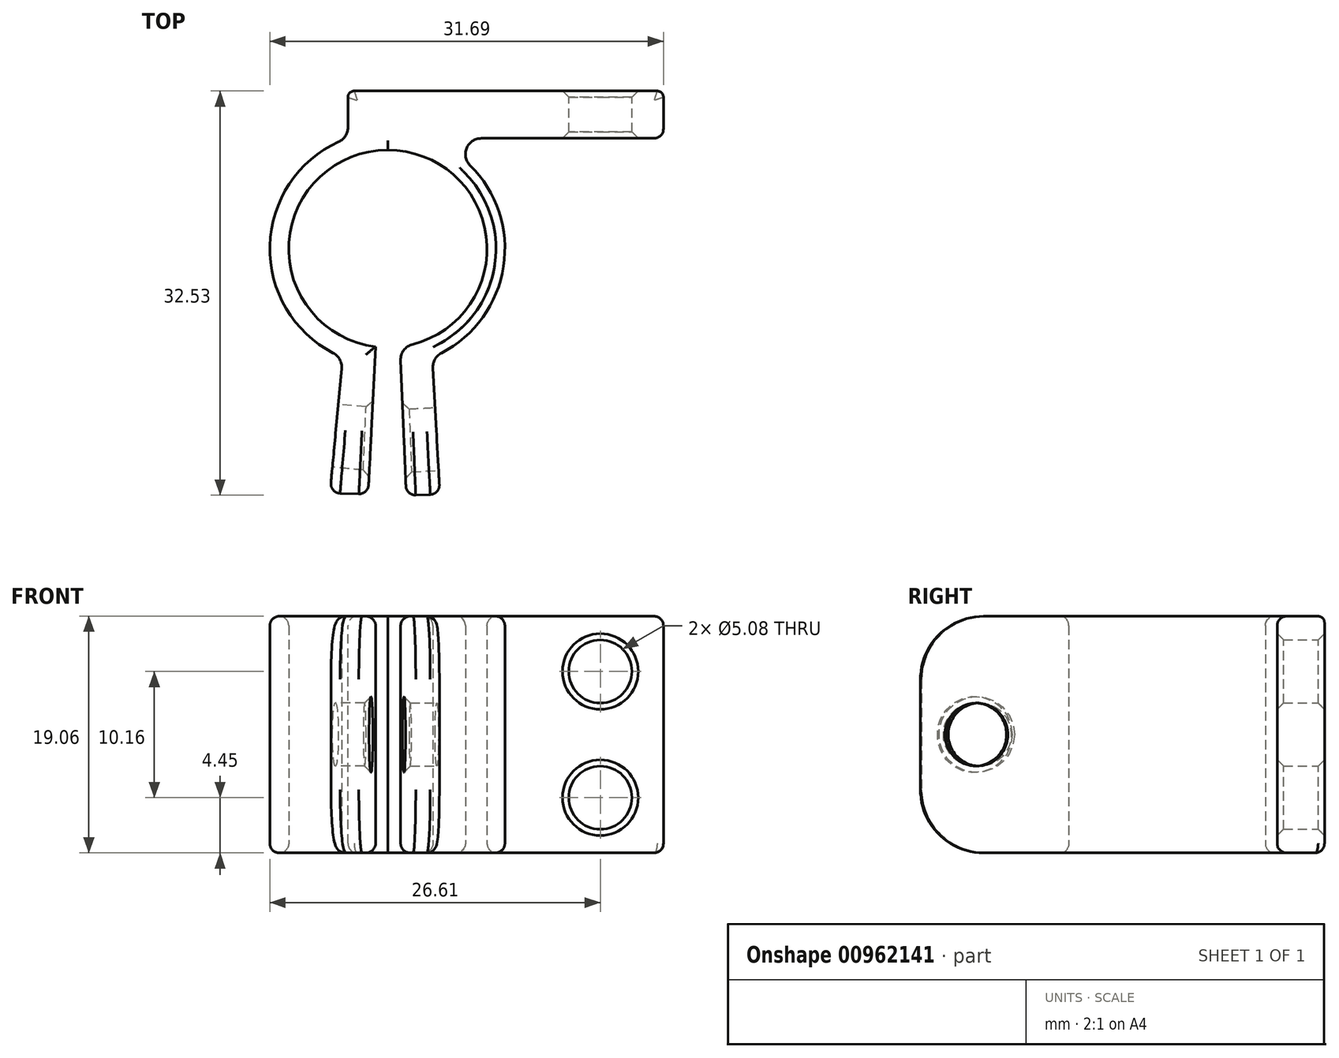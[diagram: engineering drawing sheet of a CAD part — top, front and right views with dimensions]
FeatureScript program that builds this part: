
annotation { "Feature Type Name" : "Feature", "Feature Type Description" : "" }
export const myFeature = defineFeature(function(context is Context, id is Id, definition is map)
    precondition{}
    {
        {
            var Q0;
            Q0=qCreatedBy(makeId("Front.planeOp"),FACE);
            var sketch = newSketch(context, id + "F0", { "sketchPlane" : qUnion([Q0])});
            skLineSegment(sketch, "E0.bottom", {"start": v(12.7, -9.52) * mm, "end": v(-12.7, -9.53) * mm});
            skLineSegment(sketch, "E0.top", {"start": v(12.7, 9.53) * mm, "end": v(-12.7, 9.52) * mm});
            skLineSegment(sketch, "E0.left", {"start": v(12.7, -9.52) * mm, "end": v(12.7, 9.52) * mm});
            skLineSegment(sketch, "E0.right", {"start": v(-12.7, -9.53) * mm, "end": v(-12.7, 9.53) * mm});
            skPoint(sketch, "E0.middle", {"position": v(0, 0) * mm});
            skCircle(sketch, "E1", {"center": v(7.62, 5.08) * mm, "radius": 2.54 * mm});
            skCircle(sketch, "E2.MirrorC", {"center": v(7.62, -5.08) * mm, "radius": 2.54 * mm});
            skSolve(sketch);
        }
        {
            var Q0;
            Q0 = qSketchRegion(id + "F0", true);
            extrude(context, id + "F1", {"entities" : qUnion([Q0]), "depth" : 3.8 * mm, "offsetDistance" : 25.4 * mm});
        }
        {
            var Q0;
            Q0=makeQuery(id+"F1.opExtrude","SWEPT_FACE",FACE,{"disambiguationData":[OSD([sQuery(id+"F0.wireOp",EDGE,"E0.bottom")])]});
            var sketch = newSketch(context, id + "F2", { "sketchPlane" : qUnion([Q0])});
            skLineSegment(sketch, "E3", {"start": v(-8, 32.56) * mm, "end": v(-5.3, 32.45) * mm});
            skLineSegment(sketch, "E4.trimOffspring", {"start": v(-8.5, 20.57) * mm, "end": v(-8, 32.56) * mm});
            skLineSegment(sketch, "E5.trimOffspring", {"start": v(-6, 19.81) * mm, "end": v(-6, 19.85) * mm});
            skLineSegment(sketch, "E6.MirrorCS", {"start": v(-10.47, 20.57) * mm, "end": v(-11.07, 32.46) * mm});
            skLineSegment(sketch, "E7.MirrorCS", {"start": v(-11.07, 32.46) * mm, "end": v(-14.14, 32.36) * mm});
            skLineSegment(sketch, "E8.MirrorCS", {"start": v(-12.96, 19.81) * mm, "end": v(-12.97, 19.85) * mm});
            skArc(sketch, "E9.MirrorCS", {"start": v(-8.5, 20.58) * mm, "mid": v(-1.51, 12.2) * mm, "end": v(-9.48, 4.76) * mm});
            skArc(sketch, "E10.trimOffspring", {"start": v(-13.12, 21.45) * mm, "mid": v(-9.54, 3.24) * mm, "end": v(-5.9, 21.44) * mm});
            skArc(sketch, "E11.trimOffspring", {"start": v(-10.47, 20.58) * mm, "mid": v(-17.45, 12.2) * mm, "end": v(-9.48, 4.76) * mm});
            skLineSegment(sketch, "E12.trimOffspring", {"start": v(-5.9, 21.44) * mm, "end": v(-5.3, 32.45) * mm});
            skLineSegment(sketch, "E13.trimOffspring", {"start": v(-13.12, 21.45) * mm, "end": v(-14.14, 32.36) * mm});
            skSolve(sketch);
        }
        {
            var Q0;
            Q0 = qSketchRegion(id + "F2", true);
            extrude(context, id + "F3", {"entities" : qUnion([Q0]), "operationType" : NewBodyOperationType.ADD, "oppositeDirection" : true, "depth" : 19.05 * mm, "offsetDistance" : 25.4 * mm});
        }
        {
            var Q0;
            Q0=makeQuery(id+"F3.opExtrude","SWEPT_FACE",FACE,{"disambiguationData":[OSD([sQuery(id+"F2.wireOp",EDGE,"E12.trimOffspring")])]});
            var sketch = newSketch(context, id + "F4", { "sketchPlane" : qUnion([Q0])});
            skCircle(sketch, "E14", {"center": v(-27.67, 0) * mm, "radius": 2.54 * mm});
            skPoint(sketch, "E14.centerSnap0", {"position": v(-32.11, 0) * mm});
            skSolve(sketch);
        }
        {
            var Q0;
            Q0 = qSketchRegion(id + "F4", true);
            extrude(context, id + "F5", {"entities" : qUnion([Q0]), "operationType" : NewBodyOperationType.REMOVE, "oppositeDirection" : true, "depth" : 3.17 * mm, "offsetDistance" : 25.4 * mm});
        }
        {
            var Q0;
            Q0=makeQuery(id+"F3.opExtrude","SWEPT_FACE",FACE,{"disambiguationData":[OSD([sQuery(id+"F2.wireOp",EDGE,"E13.trimOffspring")])]});
            var sketch = newSketch(context, id + "F6", { "sketchPlane" : qUnion([Q0])});
            skCircle(sketch, "E15", {"center": v(28.9, 0) * mm, "radius": 2.54 * mm});
            skSolve(sketch);
        }
        {
            var Q0;
            Q0 = qSketchRegion(id + "F6", true);
            extrude(context, id + "F7", {"entities" : qUnion([Q0]), "operationType" : NewBodyOperationType.REMOVE, "oppositeDirection" : true, "depth" : 3.17 * mm, "offsetDistance" : 25.4 * mm});
        }
        {
            var Q0;
            Q0=makeQuery(id+"F3.boolean.opBoolean","INTERSECT",EDGE,{"derivedFrom":[makeQuery(id+"F1.opExtrude","SWEPT_FACE",FACE,{"disambiguationData":[OSD([sQuery(id+"F0.wireOp",EDGE,"E0.right")])]}),makeQuery(id+"F3.opExtrude","SWEPT_FACE",FACE,{"disambiguationData":[OSD([sQuery(id+"F2.wireOp",EDGE,"E10.trimOffspring")])]})]});
            var Q1;
            Q1=makeQuery(id+"F3.opExtrude","SWEPT_EDGE",EDGE,{"disambiguationData":[OSD([sQuery(id+"F2.wireOp",EDGE,"E10.trimOffspring"),sQuery(id+"F2.wireOp",EDGE,"E13.trimOffspring")])]});
            var Q2;
            Q2=makeQuery(id+"F3.opExtrude","SWEPT_EDGE",EDGE,{"disambiguationData":[OSD([sQuery(id+"F2.wireOp",EDGE,"E4.trimOffspring"),sQuery(id+"F2.wireOp",EDGE,"E9.MirrorCS")])]});
            var Q3;
            Q3=makeQuery(id+"F3.boolean.opBoolean","INTERSECT",EDGE,{"derivedFrom":[makeQuery(id+"F1.opExtrude","CAP_FACE",FACE,{"disambiguationData":[OSD([sQuery(id+"F0.wireOp",EDGE,"E0.bottom"),sQuery(id+"F0.wireOp",EDGE,"E0.top"),sQuery(id+"F0.wireOp",EDGE,"E0.left"),sQuery(id+"F0.wireOp",EDGE,"E0.right"),sQuery(id+"F0.wireOp",EDGE,"E1"),sQuery(id+"F0.wireOp",EDGE,"E2.MirrorC")])],"isStart":false}),makeQuery(id+"F3.opExtrude","SWEPT_FACE",FACE,{"disambiguationData":[OSD([sQuery(id+"F2.wireOp",EDGE,"E10.trimOffspring")])]})]});
            var Q4;
            Q4=makeQuery(id+"F3.opExtrude","SWEPT_EDGE",EDGE,{"disambiguationData":[OSD([sQuery(id+"F2.wireOp",EDGE,"E10.trimOffspring"),sQuery(id+"F2.wireOp",EDGE,"E12.trimOffspring")])]});
            fillet(context, id + "F8", {"entities" : qUnion([Q0, Q1, Q2, Q3, Q4]), "radius" : 1.27 * mm, "tangentPropagation" : true, "allowEdgeOverflow" : false});
        }
        {
            var Q0;
            Q0=makeQuery(id+"F1.opExtrude","CAP_EDGE",EDGE,{"disambiguationData":[OSD([sQuery(id+"F0.wireOp",EDGE,"E1")])],"isStart":false});
            var Q1;
            Q1=makeQuery(id+"F1.opExtrude","CAP_EDGE",EDGE,{"disambiguationData":[OSD([sQuery(id+"F0.wireOp",EDGE,"E2.MirrorC")])],"isStart":false});
            var Q2;
            Q2=makeQuery(id+"F1.opExtrude","CAP_EDGE",EDGE,{"disambiguationData":[OSD([sQuery(id+"F0.wireOp",EDGE,"E2.MirrorC")])],"isStart":true});
            var Q3;
            Q3=makeQuery(id+"F1.opExtrude","CAP_EDGE",EDGE,{"disambiguationData":[OSD([sQuery(id+"F0.wireOp",EDGE,"E1")])],"isStart":true});
            chamfer(context, id + "F9", {"entities" : qUnion([Q0, Q1, Q2, Q3]), "width" : 0.5 * mm, "tangentPropagation" : true});
        }
        {
            var Q0;
            {var subQ0=sQuery(id+"F0.wireOp",EDGE,"E0.left");var subQ1=sQuery(id+"F0.wireOp",EDGE,"E0.bottom");Q0=makeQuery(id+"F0UlShQL8zqIgEm_1.opFillet","BLEND_EDGE",EDGE,{"blendedFrom":[makeQuery(id+"F1.opExtrude","SWEPT_EDGE",EDGE,{"disambiguationData":[OSD([subQ1,subQ0])]}),makeQuery(id+"F1.opExtrude","CAP_FACE",FACE,{"disambiguationData":[OSD([subQ1,sQuery(id+"F0.wireOp",EDGE,"E0.top"),subQ0,sQuery(id+"F0.wireOp",EDGE,"E0.right"),sQuery(id+"F0.wireOp",EDGE,"E1"),sQuery(id+"F0.wireOp",EDGE,"E2.MirrorC")])],"isStart":true})],"blendedInto":[makeQuery(id+"F1.opExtrude","CAP_FACE",FACE,{"disambiguationData":[OSD([subQ1,sQuery(id+"F0.wireOp",EDGE,"E0.top"),subQ0,sQuery(id+"F0.wireOp",EDGE,"E0.right"),sQuery(id+"F0.wireOp",EDGE,"E1"),sQuery(id+"F0.wireOp",EDGE,"E2.MirrorC")])],"isStart":true})]});}
            var Q1;
            Q1=makeQuery(id+"F1.opExtrude","CAP_EDGE",EDGE,{"disambiguationData":[OSD([sQuery(id+"F0.wireOp",EDGE,"E0.left")])],"isStart":true});
            var Q2;
            Q2=makeQuery(id+"F1.opExtrude","CAP_EDGE",EDGE,{"disambiguationData":[OSD([sQuery(id+"F0.wireOp",EDGE,"E0.top")])],"isStart":true});
            var Q3;
            Q3=makeQuery(id+"F1.opExtrude","CAP_EDGE",EDGE,{"disambiguationData":[OSD([sQuery(id+"F0.wireOp",EDGE,"E0.right")])],"isStart":true});
            var Q4;
            {var subQ0=sQuery(id+"F0.wireOp",EDGE,"E0.right");var subQ1=sQuery(id+"F0.wireOp",EDGE,"E0.bottom");Q4=makeQuery(id+"F0UlShQL8zqIgEm_1.opFillet","BLEND_EDGE",EDGE,{"blendedFrom":[makeQuery(id+"F1.opExtrude","SWEPT_EDGE",EDGE,{"disambiguationData":[OSD([subQ1,subQ0])]}),makeQuery(id+"F1.opExtrude","CAP_FACE",FACE,{"disambiguationData":[OSD([subQ1,sQuery(id+"F0.wireOp",EDGE,"E0.top"),sQuery(id+"F0.wireOp",EDGE,"E0.left"),subQ0,sQuery(id+"F0.wireOp",EDGE,"E1"),sQuery(id+"F0.wireOp",EDGE,"E2.MirrorC")])],"isStart":true})],"blendedInto":[makeQuery(id+"F1.opExtrude","CAP_FACE",FACE,{"disambiguationData":[OSD([subQ1,sQuery(id+"F0.wireOp",EDGE,"E0.top"),sQuery(id+"F0.wireOp",EDGE,"E0.left"),subQ0,sQuery(id+"F0.wireOp",EDGE,"E1"),sQuery(id+"F0.wireOp",EDGE,"E2.MirrorC")])],"isStart":true})]});}
            var Q5;
            {var subQ0=sQuery(id+"F0.wireOp",EDGE,"E0.right");var subQ1=sQuery(id+"F0.wireOp",EDGE,"E0.top");Q5=makeQuery(id+"F0UlShQL8zqIgEm_1.opFillet","BLEND_EDGE",EDGE,{"blendedFrom":[makeQuery(id+"F1.opExtrude","SWEPT_EDGE",EDGE,{"disambiguationData":[OSD([subQ1,subQ0])]}),makeQuery(id+"F1.opExtrude","CAP_FACE",FACE,{"disambiguationData":[OSD([sQuery(id+"F0.wireOp",EDGE,"E0.bottom"),subQ1,sQuery(id+"F0.wireOp",EDGE,"E0.left"),subQ0,sQuery(id+"F0.wireOp",EDGE,"E1"),sQuery(id+"F0.wireOp",EDGE,"E2.MirrorC")])],"isStart":true})],"blendedInto":[makeQuery(id+"F1.opExtrude","CAP_FACE",FACE,{"disambiguationData":[OSD([sQuery(id+"F0.wireOp",EDGE,"E0.bottom"),subQ1,sQuery(id+"F0.wireOp",EDGE,"E0.left"),subQ0,sQuery(id+"F0.wireOp",EDGE,"E1"),sQuery(id+"F0.wireOp",EDGE,"E2.MirrorC")])],"isStart":true})]});}
            fillet(context, id + "F10", {"entities" : qUnion([Q0, Q1, Q2, Q3, Q4, Q5]), "radius" : 0.5 * mm, "tangentPropagation" : true, "allowEdgeOverflow" : false});
        }
        {
            var Q0;
            Q0=makeQuery(id+"F7.boolean.opBoolean","INTERSECT",EDGE,{"derivedFrom":[makeQuery(id+"F3.opExtrude","SWEPT_FACE",FACE,{"disambiguationData":[OSD([sQuery(id+"F2.wireOp",EDGE,"E6.MirrorCS")])]}),makeQuery(id+"F7.opExtrude","SWEPT_FACE",FACE,{"disambiguationData":[OSD([sQuery(id+"F6.wireOp",EDGE,"E15")])]})]});
            var Q1;
            Q1=makeQuery(id+"F5.boolean.opBoolean","COPY",EDGE,{"derivedFrom":makeQuery(id+"F5.opExtrude","CAP_EDGE",EDGE,{"disambiguationData":[OSD([sQuery(id+"F4.wireOp",EDGE,"E14")])],"isStart":true})});
            var Q2;
            Q2=makeQuery(id+"F7.boolean.opBoolean","COPY",EDGE,{"derivedFrom":makeQuery(id+"F7.opExtrude","CAP_EDGE",EDGE,{"disambiguationData":[OSD([sQuery(id+"F6.wireOp",EDGE,"E15")])],"isStart":true})});
            var Q3;
            Q3=makeQuery(id+"F5.boolean.opBoolean","INTERSECT",EDGE,{"derivedFrom":[makeQuery(id+"F3.opExtrude","SWEPT_FACE",FACE,{"disambiguationData":[OSD([sQuery(id+"F2.wireOp",EDGE,"E4.trimOffspring")])]}),makeQuery(id+"F5.opExtrude","SWEPT_FACE",FACE,{"disambiguationData":[OSD([sQuery(id+"F4.wireOp",EDGE,"E14")])]})]});
            chamfer(context, id + "F11", {"entities" : qUnion([Q0, Q1, Q2, Q3]), "width" : 0.5 * mm, "tangentPropagation" : true});
        }
        {
            var Q0;
            Q0=makeQuery(id+"F3.opExtrude","CAP_EDGE",EDGE,{"disambiguationData":[OSD([sQuery(id+"F2.wireOp",EDGE,"E7.MirrorCS")])],"isStart":true});
            var Q1;
            Q1=makeQuery(id+"F3.opExtrude","CAP_EDGE",EDGE,{"disambiguationData":[OSD([sQuery(id+"F2.wireOp",EDGE,"E3")])],"isStart":true});
            var Q2;
            Q2=makeQuery(id+"F3.opExtrude","CAP_EDGE",EDGE,{"disambiguationData":[OSD([sQuery(id+"F2.wireOp",EDGE,"E7.MirrorCS")])],"isStart":false});
            var Q3;
            Q3=makeQuery(id+"F3.opExtrude","CAP_EDGE",EDGE,{"disambiguationData":[OSD([sQuery(id+"F2.wireOp",EDGE,"E3")])],"isStart":false});
            fillet(context, id + "F12", {"entities" : qUnion([Q0, Q1, Q2, Q3]), "radius" : 5.08 * mm, "tangentPropagation" : true, "allowEdgeOverflow" : false});
        }
        {
            var Q0;
            Q0=makeQuery(id+"F3.boolean.opBoolean","MERGE",FACE,{"derivedFrom":[makeQuery(id+"F1.opExtrude","SWEPT_FACE",FACE,{"disambiguationData":[OSD([sQuery(id+"F0.wireOp",EDGE,"E0.top")])]}),makeQuery(id+"F3.opExtrude","CAP_FACE",FACE,{"disambiguationData":[OSD([sQuery(id+"F2.wireOp",EDGE,"E3"),sQuery(id+"F2.wireOp",EDGE,"E4.trimOffspring"),sQuery(id+"F2.wireOp",EDGE,"E6.MirrorCS"),sQuery(id+"F2.wireOp",EDGE,"E7.MirrorCS"),sQuery(id+"F2.wireOp",EDGE,"E9.MirrorCS"),sQuery(id+"F2.wireOp",EDGE,"E10.trimOffspring"),sQuery(id+"F2.wireOp",EDGE,"E11.trimOffspring"),sQuery(id+"F2.wireOp",EDGE,"E12.trimOffspring"),sQuery(id+"F2.wireOp",EDGE,"E13.trimOffspring")])],"isStart":false})]});
            var Q1;
            Q1=makeQuery(id+"F3.boolean.opBoolean","MERGE",FACE,{"derivedFrom":[makeQuery(id+"F1.opExtrude","SWEPT_FACE",FACE,{"disambiguationData":[OSD([sQuery(id+"F0.wireOp",EDGE,"E0.bottom")])]}),makeQuery(id+"F3.opExtrude","CAP_FACE",FACE,{"disambiguationData":[OSD([sQuery(id+"F2.wireOp",EDGE,"E3"),sQuery(id+"F2.wireOp",EDGE,"E4.trimOffspring"),sQuery(id+"F2.wireOp",EDGE,"E6.MirrorCS"),sQuery(id+"F2.wireOp",EDGE,"E7.MirrorCS"),sQuery(id+"F2.wireOp",EDGE,"E9.MirrorCS"),sQuery(id+"F2.wireOp",EDGE,"E10.trimOffspring"),sQuery(id+"F2.wireOp",EDGE,"E11.trimOffspring"),sQuery(id+"F2.wireOp",EDGE,"E12.trimOffspring"),sQuery(id+"F2.wireOp",EDGE,"E13.trimOffspring")])],"isStart":true})]});
            var Q2;
            Q2=makeQuery(id+"F1.opExtrude","CAP_EDGE",EDGE,{"disambiguationData":[OSD([sQuery(id+"F0.wireOp",EDGE,"E0.left")])],"isStart":false});
            fillet(context, id + "F13", {"entities" : qUnion([Q0, Q1, Q2]), "radius" : 0.76 * mm, "tangentPropagation" : true, "allowEdgeOverflow" : false});
        }
    });
